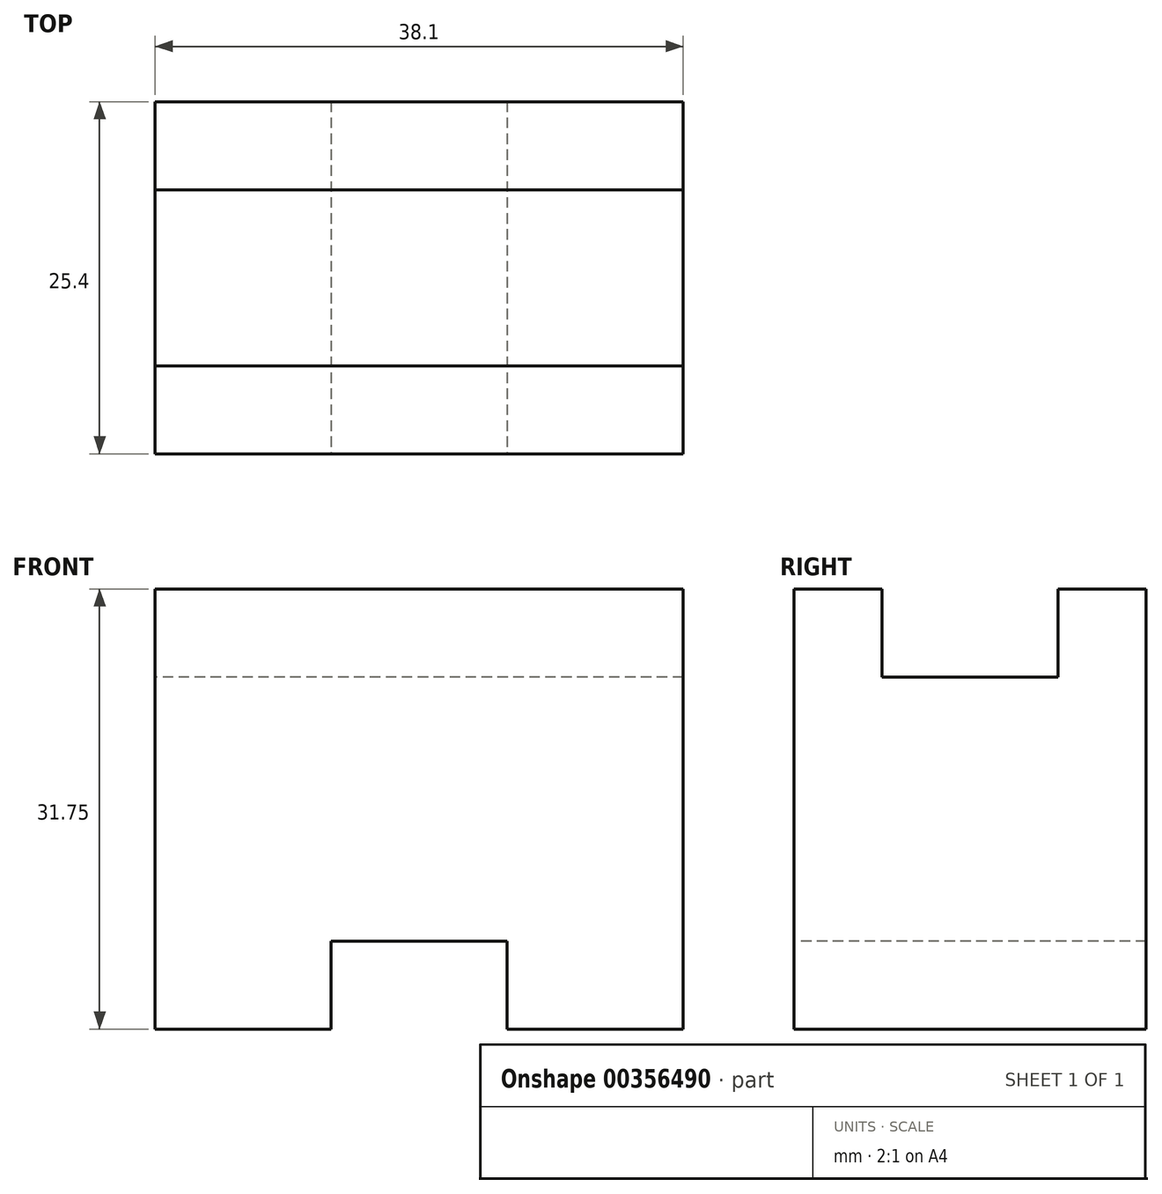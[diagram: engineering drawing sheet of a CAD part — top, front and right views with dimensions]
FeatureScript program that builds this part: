
annotation { "Feature Type Name" : "Feature", "Feature Type Description" : "" }
export const myFeature = defineFeature(function(context is Context, id is Id, definition is map)
    precondition{}
    {
        {
            var Q0;
            Q0=qCreatedBy(makeId("Right.planeOp"),FACE);
            var sketch = newSketch(context, id + "F0", { "sketchPlane" : qUnion([Q0])});
            skLineSegment(sketch, "E0", {"start": v(-25.4, 0) * mm, "end": v(0, 0) * mm});
            skLineSegment(sketch, "E1", {"start": v(0, 0) * mm, "end": v(0, 31.75) * mm});
            skLineSegment(sketch, "E2", {"start": v(-6.35, 31.75) * mm, "end": v(0, 31.75) * mm});
            skLineSegment(sketch, "E3", {"start": v(-6.35, 25.4) * mm, "end": v(-6.35, 31.75) * mm});
            skLineSegment(sketch, "E4", {"start": v(-19.05, 25.4) * mm, "end": v(-6.35, 25.4) * mm});
            skLineSegment(sketch, "E5", {"start": v(-19.05, 25.4) * mm, "end": v(-19.05, 31.75) * mm});
            skLineSegment(sketch, "E6", {"start": v(-25.4, 31.75) * mm, "end": v(-19.05, 31.75) * mm});
            skLineSegment(sketch, "E7", {"start": v(-25.4, 31.75) * mm, "end": v(-25.4, 0) * mm});
            skSolve(sketch);
        }
        {
            var Q0;
            Q0 = qSketchRegion(id + "F0", true);
            extrude(context, id + "F1", {"entities" : qUnion([Q0]), "depth" : 38.1 * mm});
        }
        {
            var Q0;
            Q0=makeQuery(id+"F1.opExtrude","SWEPT_FACE",FACE,{"disambiguationData":[OSD([sQuery(id+"F0.wireOp",EDGE,"E7")])]});
            var sketch = newSketch(context, id + "F2", { "sketchPlane" : qUnion([Q0])});
            skSolve(sketch);
        }
        {
            var Q0;
            {var subQ0=sQuery(id+"F0.wireOp",EDGE,"E7");Q0=makeQuery(id+"F2.imprint","IMPRINT",FACE,{"disambiguationData":[TD([[makeQuery(id+"F2.imprint","IMPRINT",EDGE,{"derivedFrom":makeQuery(id+"F1.opExtrude","CAP_EDGE",EDGE,{"disambiguationData":[OSD([subQ0])],"isStart":true})}),1.0]])]});}
            var sketch = newSketch(context, id + "F3", { "sketchPlane" : qUnion([Q0])});
            skLineSegment(sketch, "E8", {"start": v(0, 0) * mm, "end": v(12.7, 0) * mm});
            skLineSegment(sketch, "E9", {"start": v(12.7, 0) * mm, "end": v(12.7, 6.35) * mm});
            skLineSegment(sketch, "E10", {"start": v(12.7, 6.35) * mm, "end": v(25.4, 6.35) * mm});
            skLineSegment(sketch, "E11", {"start": v(25.4, 6.35) * mm, "end": v(25.4, 0) * mm});
            skLineSegment(sketch, "E12", {"start": v(25.4, 0) * mm, "end": v(12.7, 0) * mm});
            skLineSegment(sketch, "E13", {"start": v(25.4, 0) * mm, "end": v(38.1, 0) * mm});
            skSolve(sketch);
        }
        {
            var Q0;
            Q0 = qSketchRegion(id + "F3", true);
            extrude(context, id + "F4", {"entities" : qUnion([Q0]), "operationType" : NewBodyOperationType.REMOVE, "oppositeDirection" : true, "depth" : 25.4 * mm});
        }
    });
